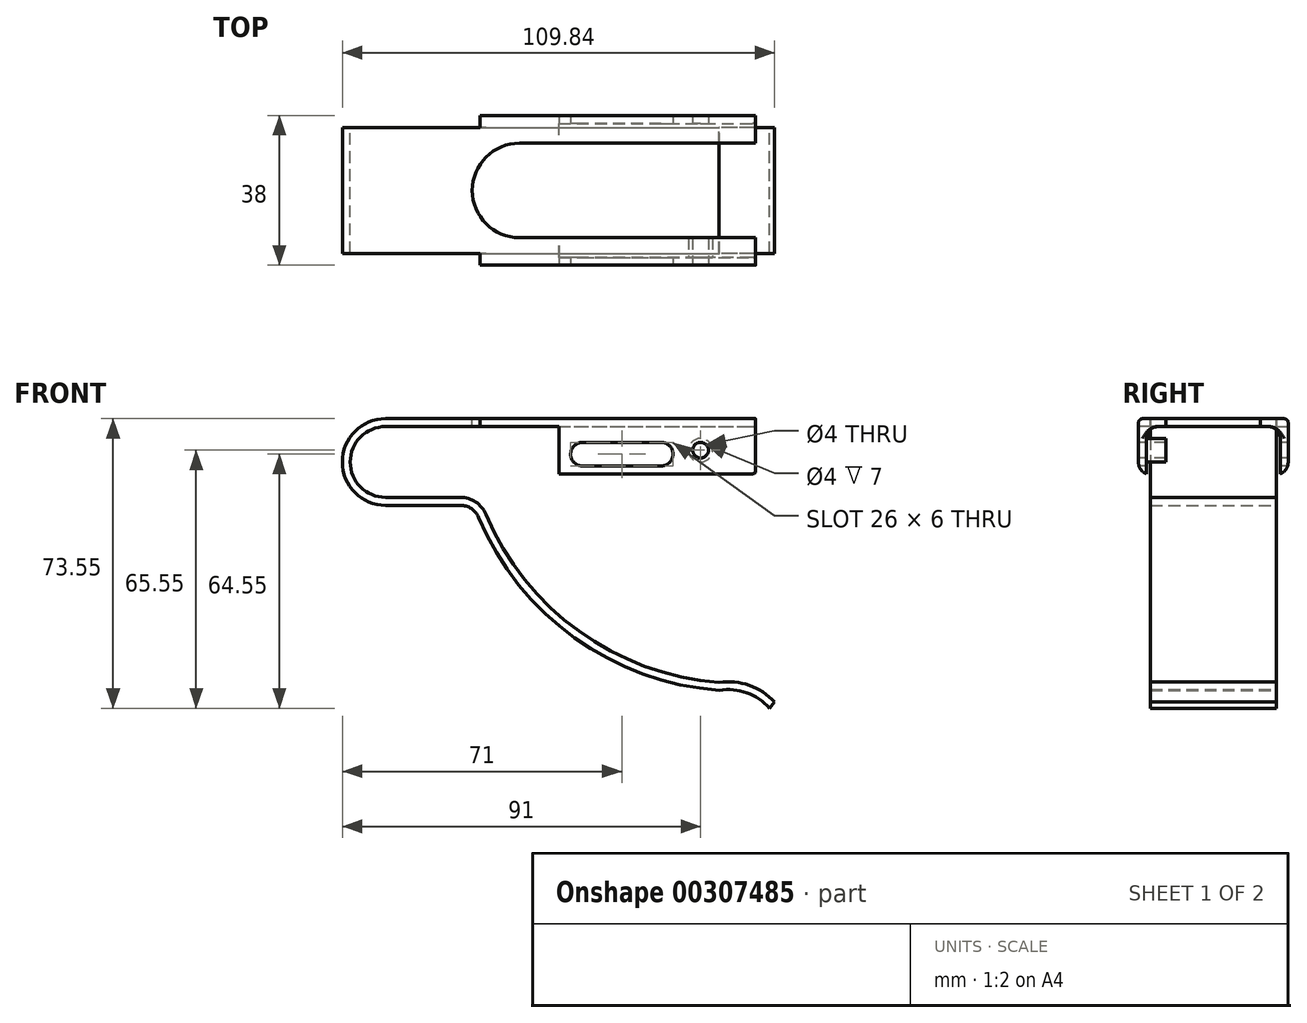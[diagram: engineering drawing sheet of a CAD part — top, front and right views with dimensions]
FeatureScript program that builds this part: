
annotation { "Feature Type Name" : "Feature", "Feature Type Description" : "" }
export const myFeature = defineFeature(function(context is Context, id is Id, definition is map)
    precondition{}
    {
        {
            var Q0;
            Q0=qCreatedBy(makeId("Front.planeOp"),FACE);
            var sketch = newSketch(context, id + "F0", { "sketchPlane" : qUnion([Q0])});
            skArc(sketch, "E0", {"start": v(0, 11) * mm, "mid": v(-11, 0) * mm, "end": v(0, -11) * mm});
            skLineSegment(sketch, "E1", {"start": v(0, 11) * mm, "end": v(94, 11) * mm});
            skLineSegment(sketch, "E2", {"start": v(0, -11) * mm, "end": v(19, -11) * mm});
            skArc(sketch, "E3", {"start": v(23.61, -14.06) * mm, "mid": v(48, -44.68) * mm, "end": v(84.78, -58.01) * mm});
            skPoint(sketch, "E4.visualSharp", {"position": v(22.4, -11) * mm});
            skArc(sketch, "E4.filletArc", {"start": v(23.61, -14.06) * mm, "mid": v(21.77, -11.84) * mm, "end": v(19, -11) * mm});
            skLineSegment(sketch, "E5.0", {"start": v(0, 9) * mm, "end": v(94, 9) * mm});
            skArc(sketch, "E5.1", {"start": v(25.45, -13.3) * mm, "mid": v(49.07, -42.99) * mm, "end": v(84.7, -56) * mm});
            skArc(sketch, "E5.2", {"start": v(25.45, -13.3) * mm, "mid": v(22.88, -10.17) * mm, "end": v(19, -9) * mm});
            skLineSegment(sketch, "E5.3", {"start": v(0, -9) * mm, "end": v(19, -9) * mm});
            skArc(sketch, "E5.4", {"start": v(0, 9) * mm, "mid": v(-9, 0) * mm, "end": v(0, -9) * mm});
            skLineSegment(sketch, "E6", {"start": v(94, 11) * mm, "end": v(94, 9) * mm});
            skArc(sketch, "E7", {"start": v(98.84, -61) * mm, "mid": v(92.4, -56.74) * mm, "end": v(84.7, -56) * mm});
            skArc(sketch, "E8.0", {"start": v(97.54, -62.55) * mm, "mid": v(91.75, -58.64) * mm, "end": v(84.78, -58.01) * mm});
            skLineSegment(sketch, "E9", {"start": v(98.84, -61) * mm, "end": v(97.54, -62.55) * mm});
            skLineSegment(sketch, "E10", {"start": v(96.33, -61) * mm, "end": v(117.8, -61) * mm});
            skSolve(sketch);
        }
        {
            var Q0;
            Q0 = qSketchRegion(id + "F0", true);
            extrude(context, id + "F1", {"entities" : qUnion([Q0]), "depth" : 16 * mm});
        }
        {
            var Q0;
            Q0=makeQuery(id+"F1.opExtrude","SWEPT_FACE",FACE,{"disambiguationData":[OSD([sQuery(id+"F0.wireOp",EDGE,"E1")])]});
            var sketch = newSketch(context, id + "F2", { "sketchPlane" : qUnion([Q0])});
            skLineSegment(sketch, "E11.bottom", {"start": v(94, -16) * mm, "end": v(24, -16) * mm});
            skLineSegment(sketch, "E11.top", {"start": v(94, -19) * mm, "end": v(24, -19) * mm});
            skLineSegment(sketch, "E11.left", {"start": v(94, -16) * mm, "end": v(94, -19) * mm});
            skLineSegment(sketch, "E11.right", {"start": v(24, -16) * mm, "end": v(24, -19) * mm});
            skSolve(sketch);
        }
        {
            var Q0;
            Q0 = qSketchRegion(id + "F2", true);
            extrude(context, id + "F3", {"entities" : qUnion([Q0]), "operationType" : NewBodyOperationType.ADD, "oppositeDirection" : true, "depth" : 2 * mm});
        }
        {
            var Q0;
            Q0=makeQuery(id+"F3.opExtrude","SWEPT_FACE",FACE,{"disambiguationData":[OSD([sQuery(id+"F2.wireOp",EDGE,"E11.top")])]});
            var sketch = newSketch(context, id + "F4", { "sketchPlane" : qUnion([Q0])});
            skLineSegment(sketch, "E12.bottom", {"start": v(94, 11) * mm, "end": v(44, 11) * mm});
            skLineSegment(sketch, "E12.top", {"start": v(94, -3) * mm, "end": v(44, -3) * mm});
            skLineSegment(sketch, "E12.left", {"start": v(94, 11) * mm, "end": v(94, -3) * mm});
            skLineSegment(sketch, "E12.right", {"start": v(44, 11) * mm, "end": v(44, -3) * mm});
            skSolve(sketch);
        }
        {
            var Q0;
            Q0 = qSketchRegion(id + "F4", true);
            extrude(context, id + "F5", {"entities" : qUnion([Q0]), "operationType" : NewBodyOperationType.ADD, "oppositeDirection" : true, "depth" : 2 * mm});
        }
        {
            var Q0;
            Q0=makeQuery(id+"F5.opExtrude","CAP_EDGE",EDGE,{"disambiguationData":[OSD([sQuery(id+"F4.wireOp",EDGE,"E12.left")])],"isStart":false});
            var Q1;
            Q1=makeQuery(id+"F3.opExtrude","CAP_EDGE",EDGE,{"disambiguationData":[OSD([sQuery(id+"F2.wireOp",EDGE,"E11.top")])],"isStart":true});
            fillet(context, id + "F6", {"entities" : qUnion([Q0, Q1]), "radius" : 1 * mm, "tangentPropagation" : true, "allowEdgeOverflow" : false});
        }
        {
            var Q0;
            Q0=makeQuery(id+"F1.opExtrude","SWEPT_BODY",BODY,{"disambiguationData":[OSD([sQuery(id+"F0.wireOp",EDGE,"E0"),sQuery(id+"F0.wireOp",EDGE,"E1"),sQuery(id+"F0.wireOp",EDGE,"E2"),sQuery(id+"F0.wireOp",EDGE,"E3"),sQuery(id+"F0.wireOp",EDGE,"E4.filletArc"),sQuery(id+"F0.wireOp",EDGE,"E5.0"),sQuery(id+"F0.wireOp",EDGE,"E5.1"),sQuery(id+"F0.wireOp",EDGE,"E5.2"),sQuery(id+"F0.wireOp",EDGE,"E5.3"),sQuery(id+"F0.wireOp",EDGE,"E5.4"),sQuery(id+"F0.wireOp",EDGE,"E6"),sQuery(id+"F0.wireOp",EDGE,"E7"),sQuery(id+"F0.wireOp",EDGE,"E8.0"),sQuery(id+"F0.wireOp",EDGE,"E9")])]});
            var Q1;
            Q1=qCreatedBy(makeId("Front.planeOp"),FACE);
            mirror(context, id + "F7", {"operationType" : NewBodyOperationType.ADD, "entities" : qUnion([Q0]), "mirrorPlane" : qUnion([Q1])});
        }
        {
            var Q0;
            {var subQ0=makeQuery(id+"F3.boolean.opBoolean","MERGE",FACE,{"derivedFrom":[makeQuery(id+"F1.opExtrude","SWEPT_FACE",FACE,{"disambiguationData":[OSD([sQuery(id+"F0.wireOp",EDGE,"E1")])]}),makeQuery(id+"F3.opExtrude","CAP_FACE",FACE,{"disambiguationData":[OSD([sQuery(id+"F2.wireOp",EDGE,"E11.bottom"),sQuery(id+"F2.wireOp",EDGE,"E11.top"),sQuery(id+"F2.wireOp",EDGE,"E11.left"),sQuery(id+"F2.wireOp",EDGE,"E11.right")])],"isStart":true})]});Q0=makeQuery(id+"F7.boolean.opBoolean","MERGE",FACE,{"derivedFrom":[subQ0,makeQuery(id+"F7.opPattern","COPY",FACE,{"derivedFrom":subQ0,"instanceName":"1"})]});}
            var sketch = newSketch(context, id + "F8", { "sketchPlane" : qUnion([Q0])});
            skArc(sketch, "E13", {"start": v(34, 12) * mm, "mid": v(22, 0) * mm, "end": v(34, -12) * mm});
            skLineSegment(sketch, "E14", {"start": v(34, 12) * mm, "end": v(94, 12) * mm});
            skLineSegment(sketch, "E15", {"start": v(34, -12) * mm, "end": v(94, -12) * mm});
            skLineSegment(sketch, "E16", {"start": v(94, 12) * mm, "end": v(94, -12) * mm});
            skSolve(sketch);
        }
        {
            var Q0;
            Q0 = qSketchRegion(id + "F8", true);
            extrude(context, id + "F9", {"entities" : qUnion([Q0]), "operationType" : NewBodyOperationType.REMOVE, "oppositeDirection" : true, "depth" : 2 * mm});
        }
        {
            var Q0;
            Q0=makeQuery(id+"F5.boolean.opBoolean","MERGE",FACE,{"derivedFrom":[makeQuery(id+"F3.opExtrude","SWEPT_FACE",FACE,{"disambiguationData":[OSD([sQuery(id+"F2.wireOp",EDGE,"E11.top")])]}),makeQuery(id+"F5.opExtrude","CAP_FACE",FACE,{"disambiguationData":[OSD([sQuery(id+"F4.wireOp",EDGE,"E12.bottom"),sQuery(id+"F4.wireOp",EDGE,"E12.top"),sQuery(id+"F4.wireOp",EDGE,"E12.left"),sQuery(id+"F4.wireOp",EDGE,"E12.right")])],"isStart":true})]});
            var sketch = newSketch(context, id + "F10", { "sketchPlane" : qUnion([Q0])});
            skLineSegment(sketch, "E17", {"start": v(50, 2) * mm, "end": v(70, 2) * mm});
            skArc(sketch, "E18.0.startCap", {"start": v(50, -1) * mm, "mid": v(47, 2) * mm, "end": v(50, 5) * mm});
            skArc(sketch, "E18.0.endCap", {"start": v(70, 5) * mm, "mid": v(73, 2) * mm, "end": v(70, -1) * mm});
            skLineSegment(sketch, "E18.0.left", {"start": v(50, 5) * mm, "end": v(70, 5) * mm});
            skLineSegment(sketch, "E18.0.right", {"start": v(50, -1) * mm, "end": v(70, -1) * mm});
            skSolve(sketch);
        }
        {
            var Q0;
            Q0 = qSketchRegion(id + "F10", true);
            extrude(context, id + "F11", {"entities" : qUnion([Q0]), "operationType" : NewBodyOperationType.REMOVE, "endBound" : BoundingType.THROUGH_ALL, "oppositeDirection" : true, "depth" : 25 * mm});
        }
        {
            var Q0;
            Q0=makeQuery(id+"F5.boolean.opBoolean","MERGE",FACE,{"derivedFrom":[makeQuery(id+"F3.opExtrude","SWEPT_FACE",FACE,{"disambiguationData":[OSD([sQuery(id+"F2.wireOp",EDGE,"E11.top")])]}),makeQuery(id+"F5.opExtrude","CAP_FACE",FACE,{"disambiguationData":[OSD([sQuery(id+"F4.wireOp",EDGE,"E12.bottom"),sQuery(id+"F4.wireOp",EDGE,"E12.top"),sQuery(id+"F4.wireOp",EDGE,"E12.left"),sQuery(id+"F4.wireOp",EDGE,"E12.right")])],"isStart":true})]});
            var sketch = newSketch(context, id + "F12", { "sketchPlane" : qUnion([Q0])});
            skPoint(sketch, "E19", {"position": v(80, 3) * mm});
            skSolve(sketch);
        }
        {
            var Q0;
            Q0=sQuery(id+"F12.wireOp",VERTEX,"E19");
            var Q1;
            Q1=makeQuery(id+"F1.opExtrude","SWEPT_BODY",BODY,{"disambiguationData":[OSD([sQuery(id+"F0.wireOp",EDGE,"E0"),sQuery(id+"F0.wireOp",EDGE,"E1"),sQuery(id+"F0.wireOp",EDGE,"E2"),sQuery(id+"F0.wireOp",EDGE,"E3"),sQuery(id+"F0.wireOp",EDGE,"E4.filletArc"),sQuery(id+"F0.wireOp",EDGE,"E5.0"),sQuery(id+"F0.wireOp",EDGE,"E5.1"),sQuery(id+"F0.wireOp",EDGE,"E5.2"),sQuery(id+"F0.wireOp",EDGE,"E5.3"),sQuery(id+"F0.wireOp",EDGE,"E5.4"),sQuery(id+"F0.wireOp",EDGE,"E6"),sQuery(id+"F0.wireOp",EDGE,"E7"),sQuery(id+"F0.wireOp",EDGE,"E8.0"),sQuery(id+"F0.wireOp",EDGE,"E9")])]});
            hole(context, id + "F13", {"style" : HoleStyle.SIMPLE, "endStyle" : HoleEndStyle.THROUGH, "holeDiameter" : 4 * mm, "isTappedThrough" : true, "tappedDepth" : 12 * mm, "tapClearance" : 3, "locations" : qUnion([Q0]), "scope" : qUnion([Q1])});
        }
        {
            var Q0;
            Q0=makeQuery(id+"F5.opExtrude","CAP_FACE",FACE,{"disambiguationData":[OSD([sQuery(id+"F4.wireOp",EDGE,"E12.bottom"),sQuery(id+"F4.wireOp",EDGE,"E12.top"),sQuery(id+"F4.wireOp",EDGE,"E12.left"),sQuery(id+"F4.wireOp",EDGE,"E12.right")])],"isStart":false});
            var sketch = newSketch(context, id + "F14", { "sketchPlane" : qUnion([Q0])});
            skCircle(sketch, "E20.0", {"center": v(-80, 3) * mm, "radius": 2 * mm});
            skCircle(sketch, "E21.0", {"center": v(-80, 3) * mm, "radius": 3 * mm});
            skSolve(sketch);
        }
        {
            var Q0;
            Q0 = qSketchRegion(id + "F14", true);
            extrude(context, id + "F15", {"entities" : qUnion([Q0]), "operationType" : NewBodyOperationType.ADD, "depth" : 5 * mm});
        }
        {
            var Q0;
            Q0=makeQuery(id+"F5.opExtrude","CAP_EDGE",EDGE,{"disambiguationData":[OSD([sQuery(id+"F4.wireOp",EDGE,"E12.top")])],"isStart":true});
            var Q1;
            Q1=makeQuery(id+"F7.opPattern","COPY",EDGE,{"derivedFrom":makeQuery(id+"F5.opExtrude","CAP_EDGE",EDGE,{"disambiguationData":[OSD([sQuery(id+"F4.wireOp",EDGE,"E12.top")])],"isStart":true}),"instanceName":"1"});
            var Q2;
            Q2=makeQuery(id+"F5.boolean.opBoolean","INTERSECT",EDGE,{"derivedFrom":[makeQuery(id+"F3.boolean.opBoolean","MERGE",FACE,{"derivedFrom":[makeQuery(id+"F1.opExtrude","SWEPT_FACE",FACE,{"disambiguationData":[OSD([sQuery(id+"F0.wireOp",EDGE,"E5.0")])]}),makeQuery(id+"F3.opExtrude","CAP_FACE",FACE,{"disambiguationData":[OSD([sQuery(id+"F2.wireOp",EDGE,"E11.bottom"),sQuery(id+"F2.wireOp",EDGE,"E11.top"),sQuery(id+"F2.wireOp",EDGE,"E11.left"),sQuery(id+"F2.wireOp",EDGE,"E11.right")])],"isStart":false})]}),makeQuery(id+"F5.opExtrude","CAP_FACE",FACE,{"disambiguationData":[OSD([sQuery(id+"F4.wireOp",EDGE,"E12.bottom"),sQuery(id+"F4.wireOp",EDGE,"E12.top"),sQuery(id+"F4.wireOp",EDGE,"E12.left"),sQuery(id+"F4.wireOp",EDGE,"E12.right")])],"isStart":false})]});
            var Q3;
            Q3=makeQuery(id+"F7.opPattern","COPY",EDGE,{"derivedFrom":makeQuery(id+"F5.boolean.opBoolean","INTERSECT",EDGE,{"derivedFrom":[makeQuery(id+"F3.boolean.opBoolean","MERGE",FACE,{"derivedFrom":[makeQuery(id+"F1.opExtrude","SWEPT_FACE",FACE,{"disambiguationData":[OSD([sQuery(id+"F0.wireOp",EDGE,"E5.0")])]}),makeQuery(id+"F3.opExtrude","CAP_FACE",FACE,{"disambiguationData":[OSD([sQuery(id+"F2.wireOp",EDGE,"E11.bottom"),sQuery(id+"F2.wireOp",EDGE,"E11.top"),sQuery(id+"F2.wireOp",EDGE,"E11.left"),sQuery(id+"F2.wireOp",EDGE,"E11.right")])],"isStart":false})]}),makeQuery(id+"F5.opExtrude","CAP_FACE",FACE,{"disambiguationData":[OSD([sQuery(id+"F4.wireOp",EDGE,"E12.bottom"),sQuery(id+"F4.wireOp",EDGE,"E12.top"),sQuery(id+"F4.wireOp",EDGE,"E12.left"),sQuery(id+"F4.wireOp",EDGE,"E12.right")])],"isStart":false})]}),"instanceName":"1"});
            fillet(context, id + "F16", {"entities" : qUnion([Q0, Q1, Q2, Q3]), "radius" : 3 * mm, "tangentPropagation" : true, "allowEdgeOverflow" : false});
        }
    });
